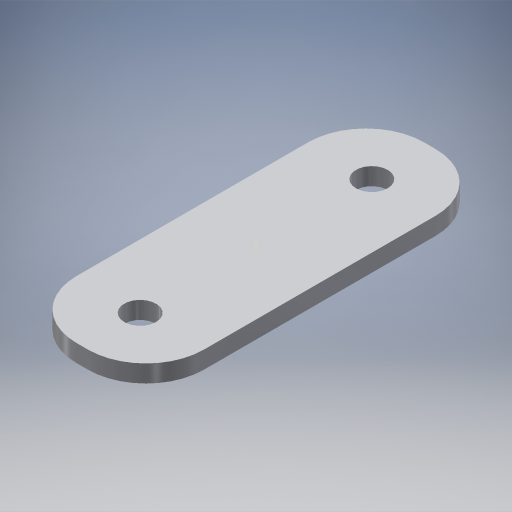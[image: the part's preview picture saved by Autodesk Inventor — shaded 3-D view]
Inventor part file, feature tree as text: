
AUTODESK INVENTOR PART (.ipt)
format: ipt  version: 2024.3 (Build 283343000, 343)  size: 254,976 bytes
history: native  units: mm
features: sketch x2, extrude x1, hole x1, fillet x1, projected_geometry x1
ambient origin geometry x8: Origin, YZ Plane, XZ Plane, XY Plane, X Axis, Y Axis, Z Axis, Center Point
bodies: Volumenkörper1 (feature_tree)
feature tree (6):
  extrude  "Extrusion1"  Depth=22.0mm
  hole  "Bohrung1"  [1 undecoded]
  fillet  "Rundung1"  Radius=10.0mm
  sketch  "Skizze3"  dims[d2=3.0mm d3=0.0mm d4=40.0mm d5=5.5mm d6=6.0mm d7=4.0mm d8=2.0mm d9=90.0deg d10=8.8mm d11=20.594885mm d12=10.0mm]
  sketch  "Skizze2"  dims[d0=60.0mm d1=22.0mm]
  projected_geometry  "Projizierte Kontur1"
note: 1 required parameter value undecoded (feature->parameter linkage not recoverable at this tier; creation-order binding heuristic only, values carry confidence <= 0.55)
